# Revit family: ARGOSQ_xx_240V_Lighting_Non-Hosted_R19
name_source: partatom
category: Lighting Fixtures
units: mm (PartAtom-declared; Revit-internal decimal feet)

## family parameters
Always vertical = Yes
Cut with Voids When Loaded = No
Light Source = Yes
OmniClass Number = 23.80.70.00
OmniClass Title = Lighting
Part Type = Normal
Room Calculation Point = No
Round Connector Dimension = Use Diameter
Shared = No
Work Plane-Based = No

## types (3) — shared parameters
Applicable Standards = AS/NZS3820, CISPR15, AS/NZS60598.1, EN 60598-2-1, BS EN IEC 55015,
BS EN 61547, BS EN IEC 61000-3-2
Color Filter = 16777215
Construction = Die-cast Aluminium Body
Diffuser = Polycarbonate Diffuser
Dimensions (L x W x H) = 321mm x 321mm x 97mm
Dimming Lamp Color Temperature Shift = <None>
Emit Shape Visible in Rendering = No
IK Rating = IK10
IP Rating = IP65
LED Driver = Clevertronics Stallion 40W
Manufacturer = Clevertronics
Mounting = Surface mount
Operating Voltage = 220-240V~ 50Hz
Photometric Web File = ARGOSQ_IESA_G_7191265393-EEC21-OCY_CIE_202108030920.IES
Power Factor = 0.91
Replacement lamp = 8050780 LED Panel: HWSUB: CT10746-D2
Supply Current = 100mA +/- 20mA
Tilt Angle = 90.00°
Weight = 3.0kg
zero-valued in all types: Default Elevation

## per-type parameters (varying)
| type | Description | Earth Leakage | Inrush Current (Max) | Lamp | MIC Number | Operating Temperature | Output Configuration | Power Consumption | Power Consumption (Standby - Lamp 10%) | Replacement Driver | Sensor | Sensor Capability | Total Lumen Output | Type Comments |
| ARGOSQ | Argonaut Square Weatherproof Non-Emergency Light | 0.35mA | 30.8A<100μs | LED Module, 4000K Cool White, Ra>80
L70/B50 Ta 40ºC; Reported >60,000hr, Projected 205,000hr
L80/B20 Ta 40ºC; Reported >60,000hr, Projected 100,000hr 
L90/B10 Ta 40ºC; Reported >43,000hr, Projected 43,000hr
LED Module, 4000K Cool White, Ra>80
L70/B50 Ta 40ºC; Reported >60,000hr, Projected 205,000hr
L80/B20 Ta 40ºC; Reported >60,000hr, Projected 100,000hr 
L90/B10 Ta 40ºC; Reported >43,000hr, Projected 43,000hr
LED Module, 4000K Cool White, Ra>80
L70/B50 Ta 40ºC; Reported >60,000hr, Projected 205,000hr
L80/B20 Ta 40ºC; Reported >60,000hr, Projected 100,000hr 
L90/B10 Ta 40ºC; Reported >43,000hr, Projected 43,000hr
LED Module, 4000K Cool White, Ra>80
L70/B50 Ta 40ºC; Reported >60,000hr, Projected 205,000hr
L80/B20 Ta 40ºC; Reported >60,000hr, Projected 100,000hr 
L90/B10 Ta 40ºC; Reported >43,000hr, Projected 43,000hr | INS04620020001 | -40˚C to 40˚C | Configurable Dual Output | 21.2W |  | 1330094 LED Driver - 40W Stallion, SP2, 470/270mA |  |  | 3242lm @ 152.9/W | Argonaut Square 240V |
| ARGOSQ-MS | Argonaut Square Weatherproof Non-Emergency Light with Motion Sensor (On/Off) | 0.33mA | 36.8A<100μs | LED module, 4000K cool white, Ra>80
L70/B50 Ta 40ºC; Reported >60,000hr, Projected 205,000hr
L80/B20 Ta 40ºC; Reported >60,000hr, Projected 100,000hr
L90/B10 Ta 40ºC; Reported >43,000hr, Projected 43,000hr | AUS04620350001 | 0˚C to 40˚C | Fixed Single Output | 21.6W |  | 1330094 LED Driver - 40W Stallion, SP2, 470/270mA | 1190312 SENSOR:M/W Motion Remote MC015S/D, Low Imped Ant | On/Off, Master Slave Capable - Yes | 3242lm @ 149.8/W | Argonaut Square 240V, MS |
| ARGOSQ-SEN | Argonaut Square Weatherproof Non-Emergency Light with Motion Sensor (Hi/Lo) | 0.33mA | 36.8A<100μs | LED module, 4000K cool white, Ra>80
L70/B50 Ta 40ºC; Reported >60,000hr, Projected 205,000hr
L80/B20 Ta 40ºC; Reported >60,000hr, Projected 100,000hr
L90/B10 Ta 40ºC; Reported >43,000hr, Projected 43,000hr | INS04620030001 | 0˚C to 40˚C | Fixed Single Output | 21.6W | 3.1W | 1330095 LED Driver - 40W Stallion, MS-HL2, 470mA | 1190133 SENSOR: Head Only, t/s MLC65-P8, GM2 Mods | High/Low, On/Off, Master Slave Capable - No | 3242lm @ 149.8lm/W | Argonaut Square 240V, SEN |

note: column(s) folded — value = type name in every type: Model

## geometry (parser evidence)
native form markers: Sweep x2
no freeform markers — native parametric forms only
